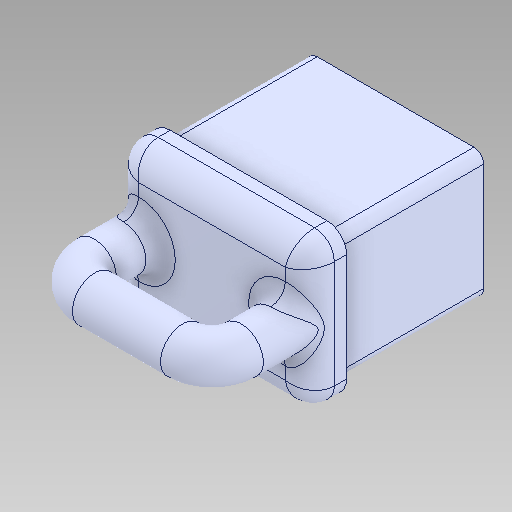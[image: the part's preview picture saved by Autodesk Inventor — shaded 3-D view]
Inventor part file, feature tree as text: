
AUTODESK INVENTOR PART (.ipt)
format: ipt  version: 2021 (Build 250183000, 183)  size: 289,280 bytes
history: native  units: in
note: dims shown in document units (in); Inventor stores cm internally (conversion verified against a paired STEP export)
features: fillet x1
ambient origin geometry x8: Origin, YZ Plane, XZ Plane, XY Plane, X Axis, Y Axis, Z Axis, Center Point
bodies: Solid1 (feature_tree)
feature tree (1):
  fillet  "Fillet2"  [1 undecoded]
note: 1 required parameter value undecoded (feature->parameter linkage not recoverable at this tier; creation-order binding heuristic only, values carry confidence <= 0.55)
